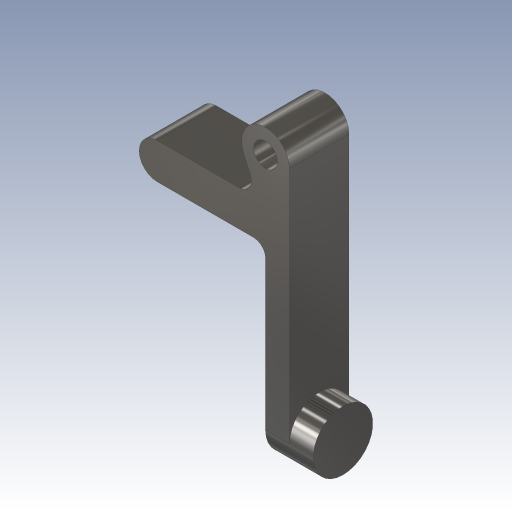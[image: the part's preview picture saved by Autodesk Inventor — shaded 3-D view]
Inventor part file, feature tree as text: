
AUTODESK INVENTOR PART (.ipt)
format: ipt  version: 2023.3 (Build 273359000, 359)  size: 174,080 bytes
history: native  units: in
note: dims shown in document units (in); Inventor stores cm internally (conversion verified against a paired STEP export)
features: fillet x2, extrude x1, sketch x1
ambient origin geometry x8: Origin, YZ Plane, XZ Plane, XY Plane, X Axis, Y Axis, Z Axis, Center Point
bodies: Body1 (feature_tree)
feature tree (4):
  extrude  "Extrusion3"  Depth=0.1575in
  fillet  "Rundung1"  Radius=0.0787in
  fillet  "Rundung2"  Radius=0.0787in
  sketch  "Skizze3"  dims[d4=0.0787in d5=0.1575in d7=0.0787in d8=0.1969in d9=0.0787in d10=0.1969in d11=0.7874in d12=0.0787in d13=0.1969in d14=0.0in d15=0.0984in d16=0.1969in d17=0.1181in d18=0.4173in d19=0.0591in d20=0.0394in]
